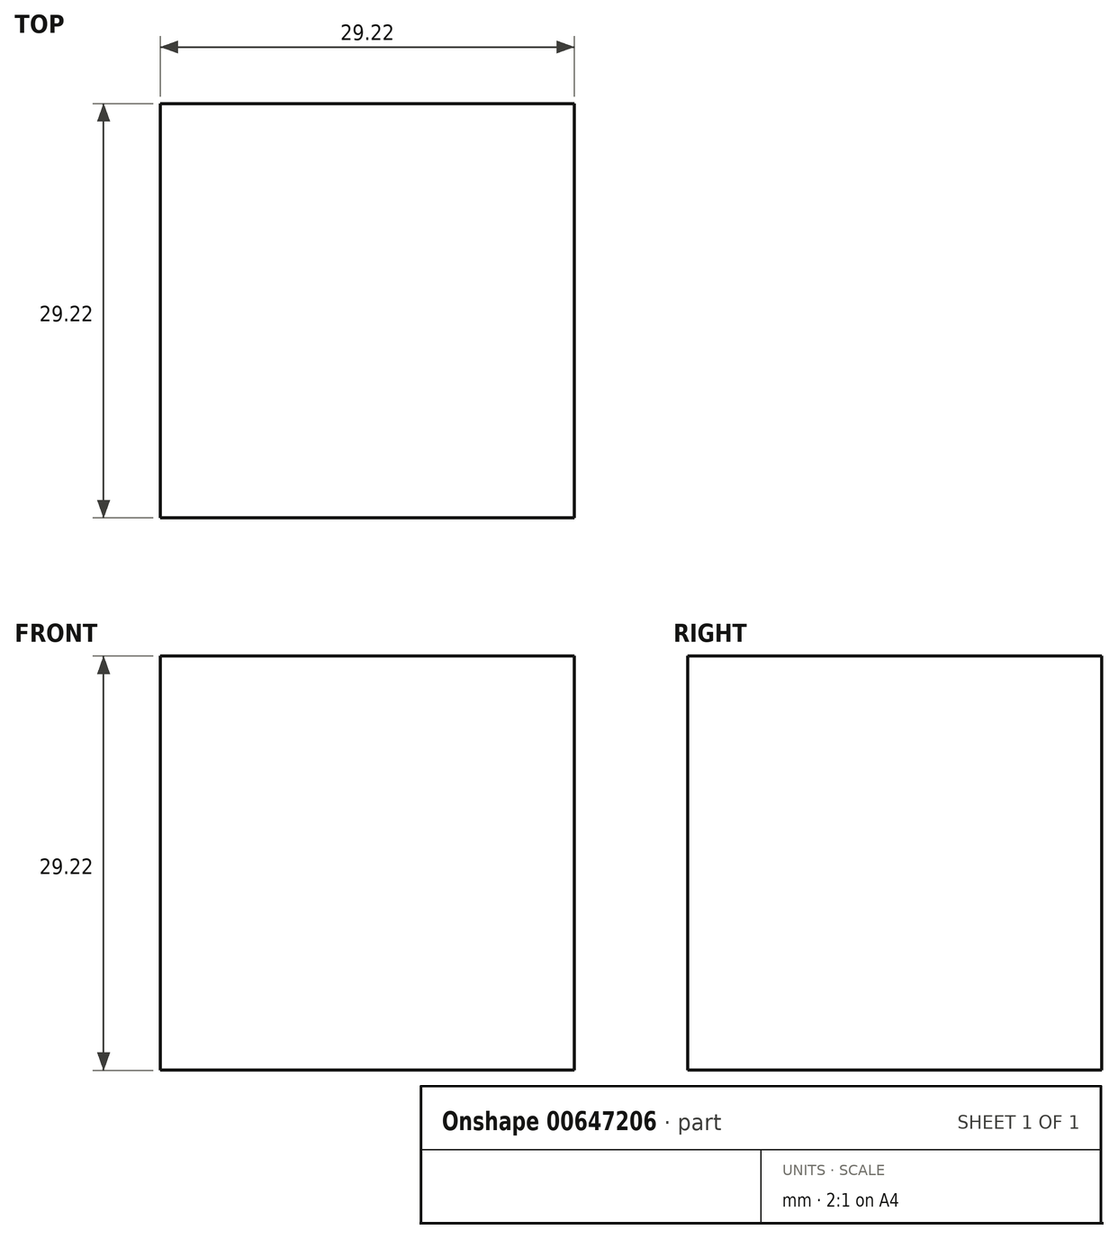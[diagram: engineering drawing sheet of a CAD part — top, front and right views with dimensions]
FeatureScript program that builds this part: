
annotation { "Feature Type Name" : "Feature", "Feature Type Description" : "" }
export const myFeature = defineFeature(function(context is Context, id is Id, definition is map)
    precondition{}
    {
        {
            var Q0;
            Q0=qCreatedBy(makeId("Front.planeOp"),FACE);
            var sketch = newSketch(context, id + "F0", { "sketchPlane" : qUnion([Q0])});
            skLineSegment(sketch, "E0.bottom", {"start": v(14.6, -14.6) * mm, "end": v(-14.6, -14.6) * mm});
            skLineSegment(sketch, "E0.top", {"start": v(14.6, 14.6) * mm, "end": v(-14.6, 14.6) * mm});
            skLineSegment(sketch, "E0.left", {"start": v(14.6, -14.6) * mm, "end": v(14.6, 14.6) * mm});
            skLineSegment(sketch, "E0.right", {"start": v(-14.6, -14.6) * mm, "end": v(-14.6, 14.6) * mm});
            skPoint(sketch, "E0.middle", {"position": v(0, 0) * mm});
            skSolve(sketch);
        }
        {
            var Q0;
            Q0 = qSketchRegion(id + "F0", true);
            extrude(context, id + "F1", {"entities" : qUnion([Q0]), "endBound" : BoundingType.SYMMETRIC, "depth" : 29.2 * mm, "offsetDistance" : 25.4 * mm});
        }
    });
